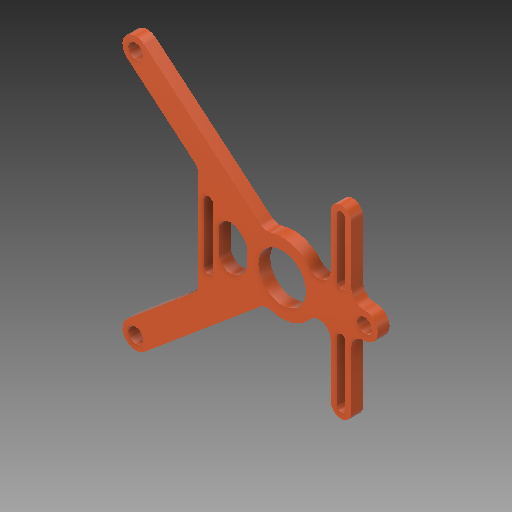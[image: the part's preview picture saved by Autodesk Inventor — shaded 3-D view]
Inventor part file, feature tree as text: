
AUTODESK INVENTOR PART (.ipt)
format: ipt  version: 2018.2 (Build 222227000, 227)  size: 219,136 bytes
history: native  units: mm
features: extrude x2, sketch x2, fillet x1
ambient origin geometry x8: Origin, YZ Plane, XZ Plane, XY Plane, X Axis, Y Axis, Z Axis, Center Point
bodies: Body1 (feature_tree)
feature tree (5):
  extrude  "Extrusion2"  Depth=5.0mm
  extrude  "Extrusion3"  Depth=28.0mm
  fillet  "Fillet1"  Radius=65.0mm
  sketch  "Sketch1"  dims[d0=24.0mm d5=5.0mm]
  sketch  "Sketch2"  dims[d6=2.0mm d7=28.0mm d8=65.0mm d9=24.43461mm d10=5.0mm d11=2.0mm d12=5.0mm d13=16.175mm d14=4.0mm d15=0.0mm d17=18.0mm d18=25.0mm d19=20.0mm d20=10.0mm d21=3.0mm d22=10.0mm d23=3.0mm d24=10.0mm d25=3.0mm d26=18.0mm d27=2.0mm d28=2.0mm d29=2.0mm d30=2.0mm d31=3.0mm d32=0.0mm d33=4.0mm]
